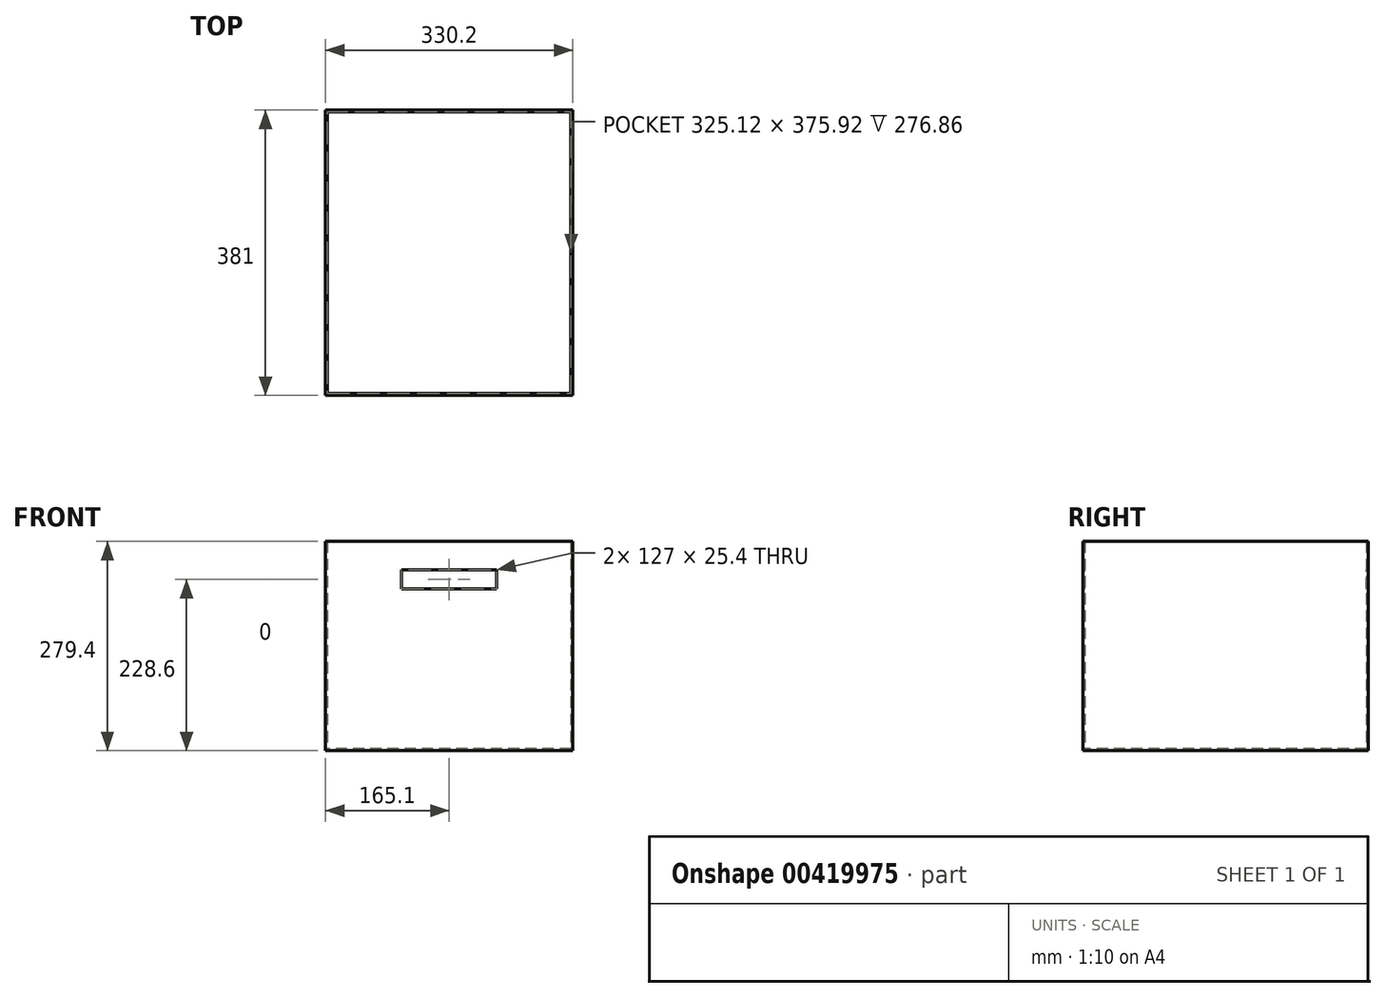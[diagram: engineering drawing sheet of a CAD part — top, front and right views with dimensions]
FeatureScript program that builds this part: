
annotation { "Feature Type Name" : "Feature", "Feature Type Description" : "" }
export const myFeature = defineFeature(function(context is Context, id is Id, definition is map)
    precondition{}
    {
        {
            var Q0;
            Q0=qCreatedBy(makeId("Top.planeOp"),FACE);
            var sketch = newSketch(context, id + "F0", { "sketchPlane" : qUnion([Q0])});
            skLineSegment(sketch, "E0.bottom", {"start": v(165.1, 190.5) * mm, "end": v(-165.1, 190.5) * mm});
            skLineSegment(sketch, "E0.top", {"start": v(165.1, -190.5) * mm, "end": v(-165.1, -190.5) * mm});
            skLineSegment(sketch, "E0.left", {"start": v(165.1, 190.5) * mm, "end": v(165.1, -190.5) * mm});
            skLineSegment(sketch, "E0.right", {"start": v(-165.1, 190.5) * mm, "end": v(-165.1, -190.5) * mm});
            skPoint(sketch, "E0.middle", {"position": v(0, 0) * mm});
            skSolve(sketch);
        }
        {
            var Q0;
            Q0 = qSketchRegion(id + "F0", true);
            extrude(context, id + "F1", {"entities" : qUnion([Q0]), "offsetDistance" : 25.4 * mm, "depth" : 279.4 * mm});
        }
        {
            var Q0;
            Q0=makeQuery(id+"F1.opExtrude","CAP_FACE",FACE,{"disambiguationData":[OSD([sQuery(id+"F0.wireOp",EDGE,"E0.bottom"),sQuery(id+"F0.wireOp",EDGE,"E0.top"),sQuery(id+"F0.wireOp",EDGE,"E0.left"),sQuery(id+"F0.wireOp",EDGE,"E0.right")])],"isStart":false});
            shell(context, id + "F2", {"entities" : qUnion([Q0]), "thickness" : 2.54 * mm});
        }
        {
            var Q0;
            Q0=makeQuery(id+"F1.opExtrude","SWEPT_FACE",FACE,{"disambiguationData":[OSD([sQuery(id+"F0.wireOp",EDGE,"E0.top")])]});
            var sketch = newSketch(context, id + "F3", { "sketchPlane" : qUnion([Q0])});
            skLineSegment(sketch, "E1.bottom", {"start": v(63.5, 215.9) * mm, "end": v(-63.5, 215.9) * mm});
            skLineSegment(sketch, "E1.top", {"start": v(63.5, 241.3) * mm, "end": v(-63.5, 241.3) * mm});
            skLineSegment(sketch, "E1.left", {"start": v(63.5, 215.9) * mm, "end": v(63.5, 241.3) * mm});
            skLineSegment(sketch, "E1.right", {"start": v(-63.5, 215.9) * mm, "end": v(-63.5, 241.3) * mm});
            skPoint(sketch, "E1.middle", {"position": v(0, 228.6) * mm});
            skSolve(sketch);
        }
        {
            var Q0;
            Q0 = qSketchRegion(id + "F3", true);
            extrude(context, id + "F4", {"entities" : qUnion([Q0]), "operationType" : NewBodyOperationType.REMOVE, "endBound" : BoundingType.THROUGH_ALL, "oppositeDirection" : true, "depth" : 25.4 * mm});
        }
    });
